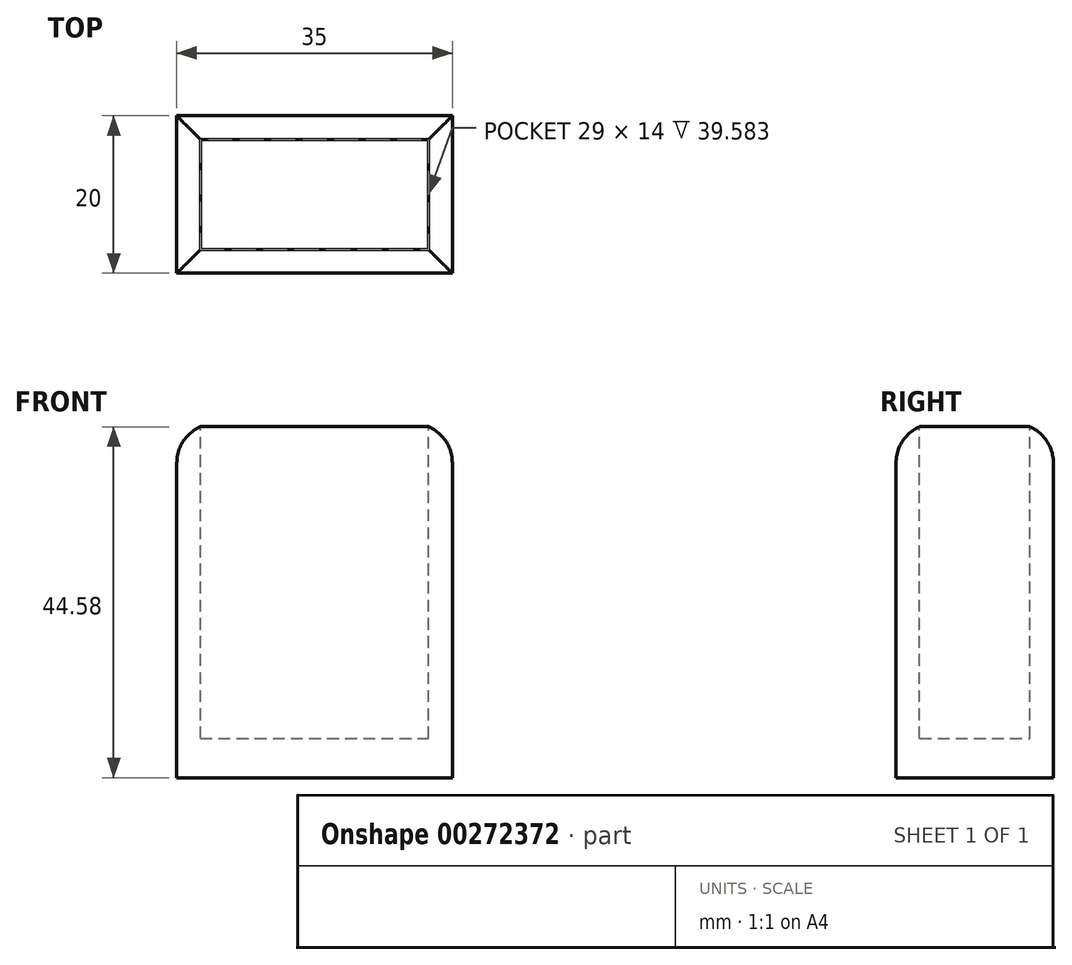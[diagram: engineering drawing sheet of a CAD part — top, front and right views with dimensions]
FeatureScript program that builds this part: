
annotation { "Feature Type Name" : "Feature", "Feature Type Description" : "" }
export const myFeature = defineFeature(function(context is Context, id is Id, definition is map)
    precondition{}
    {
        {
            var Q0;
            Q0=qCreatedBy(makeId("Top.planeOp"),FACE);
            var sketch = newSketch(context, id + "F0", { "sketchPlane" : qUnion([Q0])});
            skLineSegment(sketch, "E0.bottom", {"start": v(17.5, -10) * mm, "end": v(-17.5, -10) * mm});
            skLineSegment(sketch, "E0.top", {"start": v(17.5, 10) * mm, "end": v(-17.5, 10) * mm});
            skLineSegment(sketch, "E0.left", {"start": v(17.5, -10) * mm, "end": v(17.5, 10) * mm});
            skLineSegment(sketch, "E0.right", {"start": v(-17.5, -10) * mm, "end": v(-17.5, 10) * mm});
            skPoint(sketch, "E0.middle", {"position": v(0, 0) * mm});
            skSolve(sketch);
        }
        {
            var Q0;
            Q0 = qSketchRegion(id + "F0", true);
            extrude(context, id + "F1", {"entities" : qUnion([Q0]), "depth" : 45 * mm});
        }
        {
            var Q0;
            Q0=makeQuery(id+"F1.opExtrude","CAP_FACE",FACE,{"disambiguationData":[OSD([sQuery(id+"F0.wireOp",EDGE,"E0.bottom"),sQuery(id+"F0.wireOp",EDGE,"E0.top"),sQuery(id+"F0.wireOp",EDGE,"E0.left"),sQuery(id+"F0.wireOp",EDGE,"E0.right")])],"isStart":false});
            var sketch = newSketch(context, id + "F2", { "sketchPlane" : qUnion([Q0])});
            skLineSegment(sketch, "E1.0", {"start": v(14.5, -7) * mm, "end": v(14.5, 7) * mm});
            skLineSegment(sketch, "E1.1", {"start": v(-14.5, -7) * mm, "end": v(14.5, -7) * mm});
            skLineSegment(sketch, "E1.2", {"start": v(-14.5, 7) * mm, "end": v(-14.5, -7) * mm});
            skLineSegment(sketch, "E1.3", {"start": v(14.5, 7) * mm, "end": v(-14.5, 7) * mm});
            skSolve(sketch);
        }
        {
            var Q0;
            Q0=makeQuery(id+"F2.imprint","IMPRINT",FACE,{"disambiguationData":[TD([[makeQuery(id+"F2.imprint","IMPRINT",EDGE,{"derivedFrom":sQuery(id+"F2.wireOp",EDGE,"E1.0")}),1.0]])]});
            extrude(context, id + "F3", {"entities" : qUnion([Q0]), "operationType" : NewBodyOperationType.REMOVE, "oppositeDirection" : true, "depth" : 40 * mm});
        }
        {
            var Q0;
            Q0=makeQuery(id+"F1.opExtrude","CAP_EDGE",EDGE,{"disambiguationData":[OSD([sQuery(id+"F0.wireOp",EDGE,"E0.bottom")])],"isStart":false});
            var Q1;
            Q1=makeQuery(id+"F1.opExtrude","CAP_EDGE",EDGE,{"disambiguationData":[OSD([sQuery(id+"F0.wireOp",EDGE,"E0.right")])],"isStart":false});
            var Q2;
            Q2=makeQuery(id+"F1.opExtrude","CAP_EDGE",EDGE,{"disambiguationData":[OSD([sQuery(id+"F0.wireOp",EDGE,"E0.top")])],"isStart":false});
            var Q3;
            Q3=makeQuery(id+"F1.opExtrude","CAP_EDGE",EDGE,{"disambiguationData":[OSD([sQuery(id+"F0.wireOp",EDGE,"E0.left")])],"isStart":false});
            fillet(context, id + "F4", {"entities" : qUnion([Q0, Q1, Q2, Q3]), "radius" : 5 * mm, "tangentPropagation" : true, "allowEdgeOverflow" : false});
        }
    });
